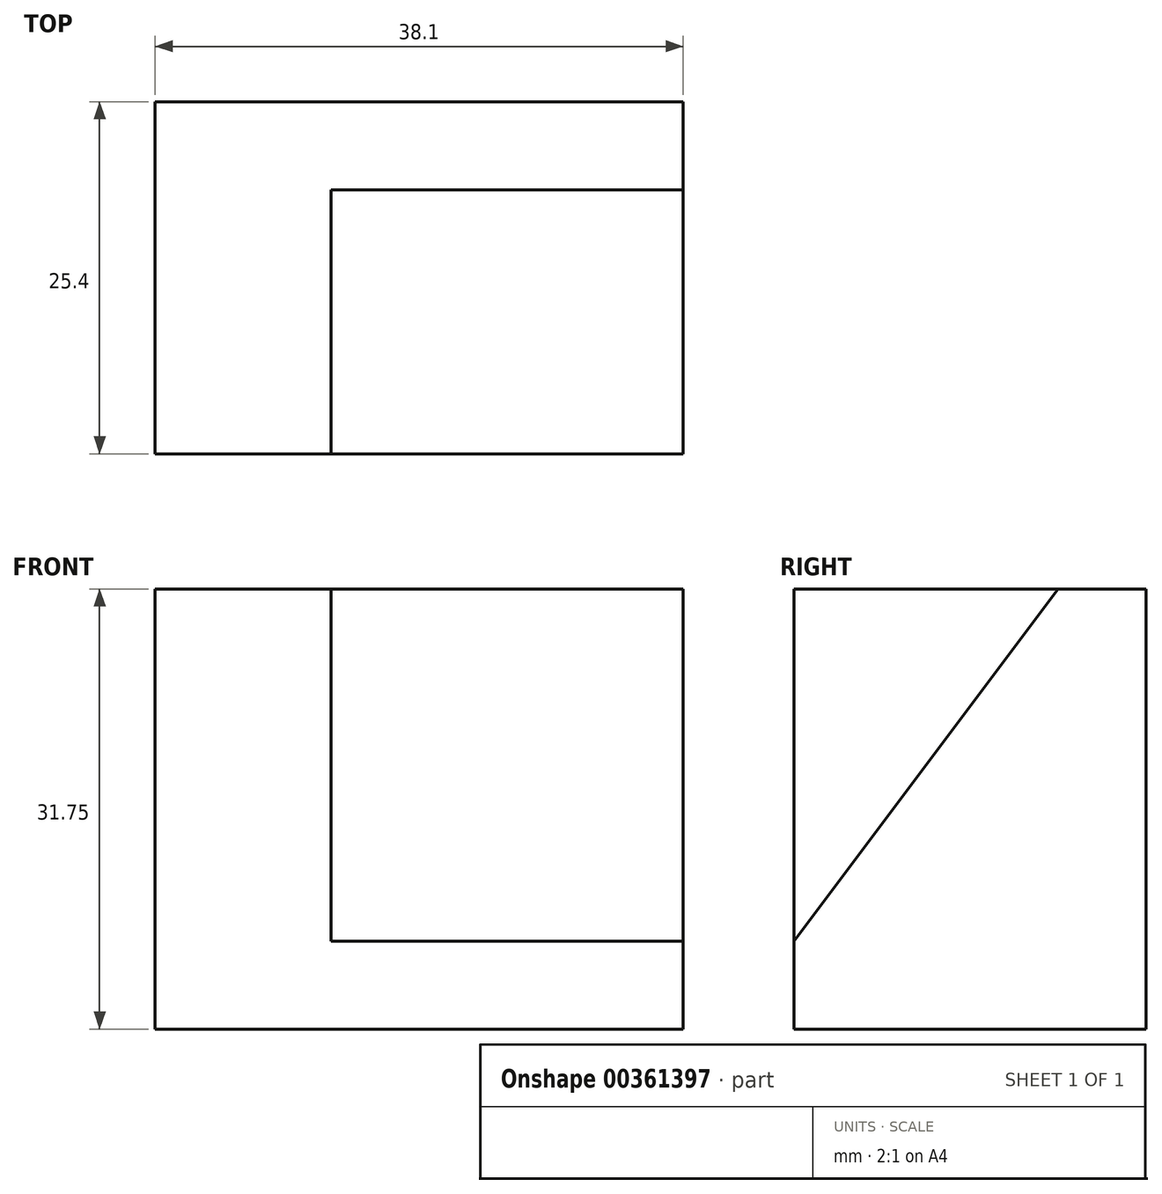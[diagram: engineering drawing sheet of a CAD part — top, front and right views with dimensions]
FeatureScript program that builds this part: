
annotation { "Feature Type Name" : "Feature", "Feature Type Description" : "" }
export const myFeature = defineFeature(function(context is Context, id is Id, definition is map)
    precondition{}
    {
        {
            var Q0;
            Q0=qCreatedBy(makeId("Right.planeOp"),FACE);
            var sketch = newSketch(context, id + "F0", { "sketchPlane" : qUnion([Q0])});
            skLineSegment(sketch, "E0", {"start": v(0, 0) * mm, "end": v(-25.4, 0) * mm});
            skLineSegment(sketch, "E1", {"start": v(0, 0) * mm, "end": v(0, 31.75) * mm});
            skLineSegment(sketch, "E2", {"start": v(0, 31.75) * mm, "end": v(-6.35, 31.75) * mm});
            skLineSegment(sketch, "E3", {"start": v(-25.4, 0) * mm, "end": v(-25.4, 6.35) * mm});
            skLineSegment(sketch, "E4", {"start": v(-25.4, 6.35) * mm, "end": v(-6.35, 31.75) * mm});
            skSolve(sketch);
        }
        {
            var Q0;
            Q0 = qSketchRegion(id + "F0", true);
            extrude(context, id + "F1", {"entities" : qUnion([Q0]), "depth" : 38.1 * mm});
        }
        {
            var Q0;
            Q0=makeQuery(id+"F1.opExtrude","CAP_FACE",FACE,{"disambiguationData":[OSD([sQuery(id+"F0.wireOp",EDGE,"E0"),sQuery(id+"F0.wireOp",EDGE,"E1"),sQuery(id+"F0.wireOp",EDGE,"E2"),sQuery(id+"F0.wireOp",EDGE,"E3"),sQuery(id+"F0.wireOp",EDGE,"E4")])],"isStart":true});
            var sketch = newSketch(context, id + "F2", { "sketchPlane" : qUnion([Q0])});
            skLineSegment(sketch, "E5", {"start": v(25.4, 6.35) * mm, "end": v(25.4, 31.75) * mm});
            skLineSegment(sketch, "E6", {"start": v(25.4, 31.75) * mm, "end": v(6.35, 31.75) * mm});
            skLineSegment(sketch, "E7", {"start": v(6.35, 31.75) * mm, "end": v(25.4, 6.35) * mm});
            skSolve(sketch);
        }
        {
            var Q0;
            Q0 = qSketchRegion(id + "F2", true);
            extrude(context, id + "F3", {"entities" : qUnion([Q0]), "operationType" : NewBodyOperationType.ADD, "oppositeDirection" : true, "depth" : 12.7 * mm});
        }
    });
